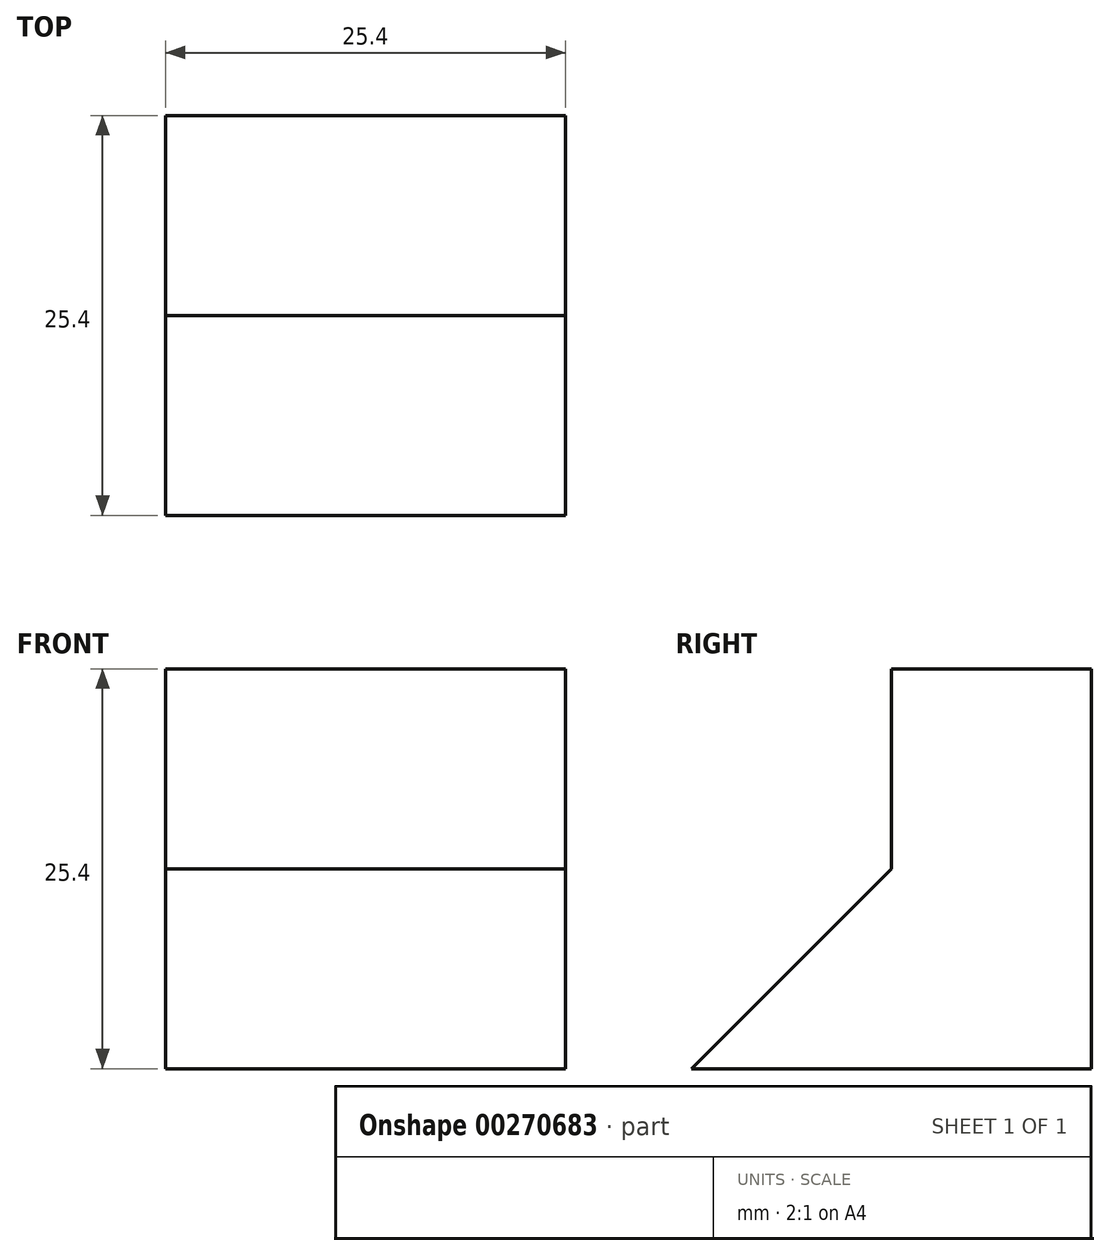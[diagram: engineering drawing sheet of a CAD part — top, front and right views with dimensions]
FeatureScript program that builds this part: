
annotation { "Feature Type Name" : "Feature", "Feature Type Description" : "" }
export const myFeature = defineFeature(function(context is Context, id is Id, definition is map)
    precondition{}
    {
        {
            var Q0;
            Q0=qCreatedBy(makeId("Front.planeOp"),FACE);
            var sketch = newSketch(context, id + "F0", { "sketchPlane" : qUnion([Q0])});
            skLineSegment(sketch, "E0.bottom", {"start": v(0, 0) * mm, "end": v(-25.4, 0) * mm});
            skLineSegment(sketch, "E0.top", {"start": v(0, 25.4) * mm, "end": v(-25.4, 25.4) * mm});
            skLineSegment(sketch, "E0.left", {"start": v(0, 0) * mm, "end": v(0, 25.4) * mm});
            skLineSegment(sketch, "E0.right", {"start": v(-25.4, 0) * mm, "end": v(-25.4, 25.4) * mm});
            skSolve(sketch);
        }
        {
            var Q0;
            Q0=makeQuery(id+"F0.imprint","IMPRINT",FACE,{"disambiguationData":[TD([[makeQuery(id+"F0.imprint","IMPRINT",EDGE,{"derivedFrom":sQuery(id+"F0.wireOp",EDGE,"E0.bottom")}),-1.0]])]});
            extrude(context, id + "F1", {"entities" : qUnion([Q0]), "depth" : 25.4 * mm});
        }
        {
            var Q0;
            Q0=makeQuery(id+"F1.opExtrude","SWEPT_FACE",FACE,{"disambiguationData":[OSD([sQuery(id+"F0.wireOp",EDGE,"E0.right")])]});
            var sketch = newSketch(context, id + "F2", { "sketchPlane" : qUnion([Q0])});
            skLineSegment(sketch, "E1", {"start": v(25.4, 0) * mm, "end": v(12.7, 12.7) * mm});
            skPoint(sketch, "E1.endSnap0", {"position": v(0, 12.7) * mm});
            skPoint(sketch, "E1.endSnap1", {"position": v(12.7, 0) * mm});
            skLineSegment(sketch, "E2", {"start": v(12.7, 12.7) * mm, "end": v(12.7, 25.4) * mm});
            skLineSegment(sketch, "E3", {"start": v(12.7, 25.4) * mm, "end": v(12.7, 12.7) * mm});
            skSolve(sketch);
        }
        {
            var Q0;
            Q0=makeQuery(id+"F2.imprint","IMPRINT",FACE,{"disambiguationData":[TD([[makeQuery(id+"F2.imprint","IMPRINT",EDGE,{"derivedFrom":sQuery(id+"F2.wireOp",EDGE,"E1")}),-1.0]])]});
            extrude(context, id + "F3", {"entities" : qUnion([Q0]), "operationType" : NewBodyOperationType.REMOVE, "oppositeDirection" : true, "depth" : 25.4 * mm});
        }
    });
